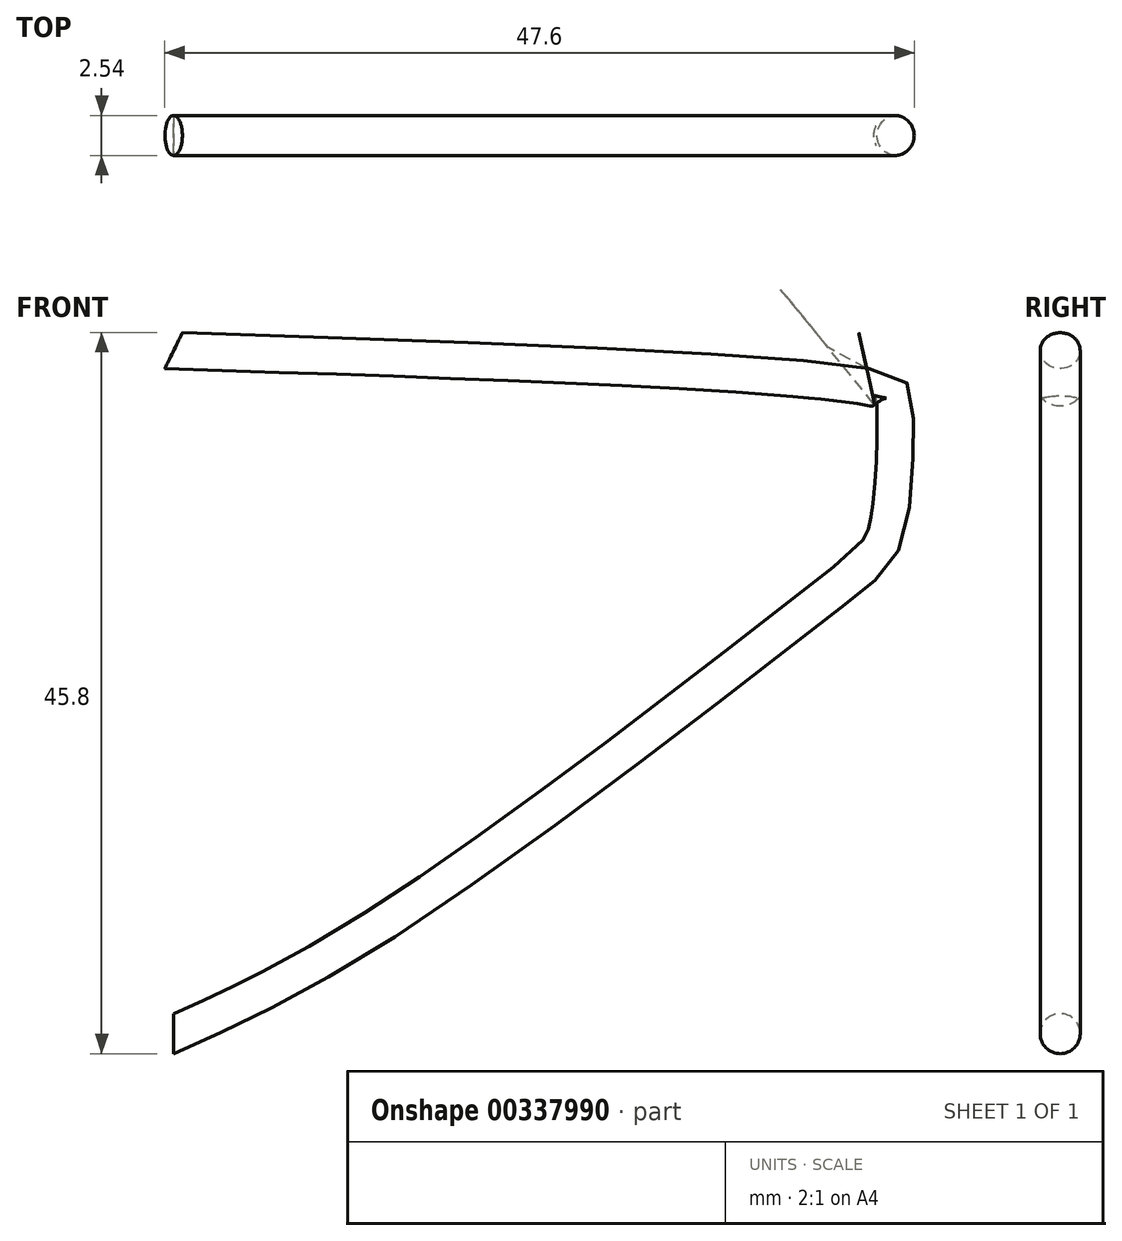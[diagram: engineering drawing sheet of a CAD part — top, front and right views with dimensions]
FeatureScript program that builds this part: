
annotation { "Feature Type Name" : "Feature", "Feature Type Description" : "" }
export const myFeature = defineFeature(function(context is Context, id is Id, definition is map)
    precondition{}
    {
        {
            var Q0;
            Q0=qCreatedBy(makeId("Front.planeOp"),FACE);
            var sketch = newSketch(context, id + "F0", { "sketchPlane" : qUnion([Q0])});
            skFitSpline(sketch, "E0", {"points": [v(0, 0) * mm, v(14.16, 7.6) * mm, v(42.2, 28.4) * mm, v(45.34, 32.27) * mm, v(45.83, 39.76) * mm, v(45.34, 40.73) * mm, v(0, 43.39) * mm], "startDerivative": vector(67.88, 30.38) * mm, "endDerivative": vector(-213.97, 6.97) * mm});
            skSolve(sketch);
        }
        {
            var Q0;
            Q0=qCreatedBy(makeId("Right.planeOp"),FACE);
            var sketch = newSketch(context, id + "F1", { "sketchPlane" : qUnion([Q0])});
            skCircle(sketch, "E1", {"center": v(0, 0) * mm, "radius": 1.27 * mm});
            skSolve(sketch);
        }
        {
            var Q0;
            Q0=makeQuery(id+"F1.imprint","IMPRINT",FACE,{"disambiguationData":[TD([[makeQuery(id+"F1.imprint","IMPRINT",EDGE,{"derivedFrom":sQuery(id+"F1.wireOp",EDGE,"E1")}),1.0]])]});
            var Q1;
            Q1=sQuery(id+"F0.wireOp",EDGE,"E0");
            sweep(context, id + "F2", {"profiles" : qUnion([Q0]), "path" : qUnion([Q1])});
        }
    });
